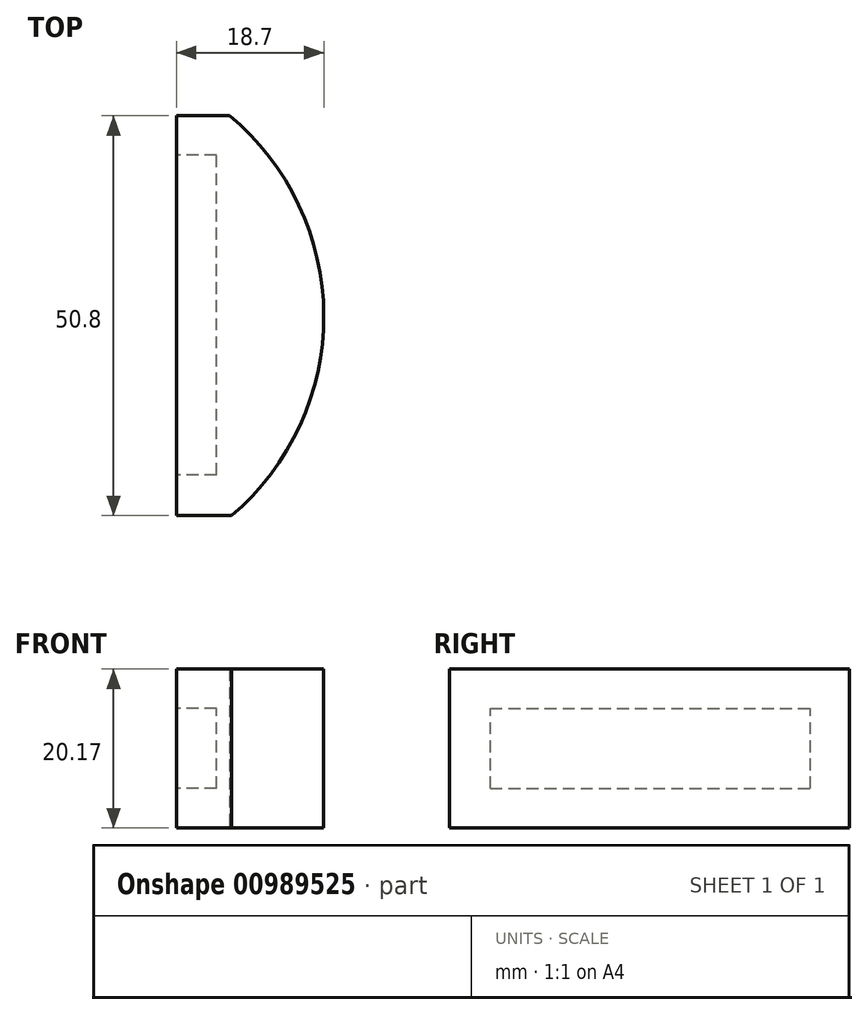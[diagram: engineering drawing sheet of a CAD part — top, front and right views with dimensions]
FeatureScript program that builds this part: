
annotation { "Feature Type Name" : "Feature", "Feature Type Description" : "" }
export const myFeature = defineFeature(function(context is Context, id is Id, definition is map)
    precondition{}
    {
        {
            assignVariable(context, id + "F0", {"variableType" : VariableType.LENGTH, "name" : "boarder", "lengthValue" : 10.16 * mm});
        }
        {
            var Q0;
            Q0=qCreatedBy(makeId("Top.planeOp"),FACE);
            var sketch = newSketch(context, id + "F1", { "sketchPlane" : qUnion([Q0])});
            skLineSegment(sketch, "E0", {"start": v(0, 25.4) * mm, "end": v(0, -25.4) * mm});
            skLineSegment(sketch, "E1", {"start": v(0, -25.4) * mm, "end": v(6.99, -25.4) * mm});
            skLineSegment(sketch, "E2", {"start": v(0, 25.4) * mm, "end": v(6.73, 25.4) * mm});
            skArc(sketch, "E3", {"start": v(6.99, -25.4) * mm, "mid": v(18.7, 0.06) * mm, "end": v(6.73, 25.4) * mm});
            skSolve(sketch);
        }
        {
            var Q0;
            Q0=makeQuery(id+"F1.imprint","IMPRINT",FACE,{"disambiguationData":[TD([[makeQuery(id+"F1.imprint","IMPRINT",EDGE,{"derivedFrom":sQuery(id+"F1.wireOp",EDGE,"E0")}),1.0]])]});
            extrude(context, id + "F2", {"entities" : qUnion([Q0]), "depth" : 10 * mm + getVariable(context, 'boarder'), "offsetDistance" : 25.4 * mm});
        }
        {
            var Q0;
            Q0=makeQuery(id+"F2.opExtrude","SWEPT_FACE",FACE,{"disambiguationData":[OSD([sQuery(id+"F1.wireOp",EDGE,"E0")])]});
            var sketch = newSketch(context, id + "F3", { "sketchPlane" : qUnion([Q0])});
            skLineSegment(sketch, "E4.bottom", {"start": v(20.24, 5) * mm, "end": v(-20.4, 5) * mm});
            skLineSegment(sketch, "E4.top", {"start": v(20.24, 15.16) * mm, "end": v(-20.4, 15.16) * mm});
            skLineSegment(sketch, "E4.left", {"start": v(20.24, 5) * mm, "end": v(20.24, 15.16) * mm});
            skLineSegment(sketch, "E4.right", {"start": v(-20.4, 5) * mm, "end": v(-20.4, 15.16) * mm});
            skLineSegment(sketch, "E5", {"start": v(20.24, 15.16) * mm, "end": v(20.24, 20.17) * mm, "construction": true});
            skLineSegment(sketch, "E6", {"start": v(-20.4, 15.16) * mm, "end": v(-25.4, 15.16) * mm, "construction": true});
            skLineSegment(sketch, "E7", {"start": v(-20.4, 5) * mm, "end": v(-20.4, 0) * mm, "construction": true});
            skSolve(sketch);
        }
        {
            var Q0;
            Q0=makeQuery(id+"F3.imprint","IMPRINT",FACE,{"disambiguationData":[TD([[makeQuery(id+"F3.imprint","IMPRINT",EDGE,{"derivedFrom":sQuery(id+"F3.wireOp",EDGE,"E4.bottom")}),-1.0]])]});
            extrude(context, id + "F4", {"entities" : qUnion([Q0]), "operationType" : NewBodyOperationType.REMOVE, "oppositeDirection" : true, "depth" : 5.08 * mm, "offsetDistance" : 25.4 * mm});
        }
    });
